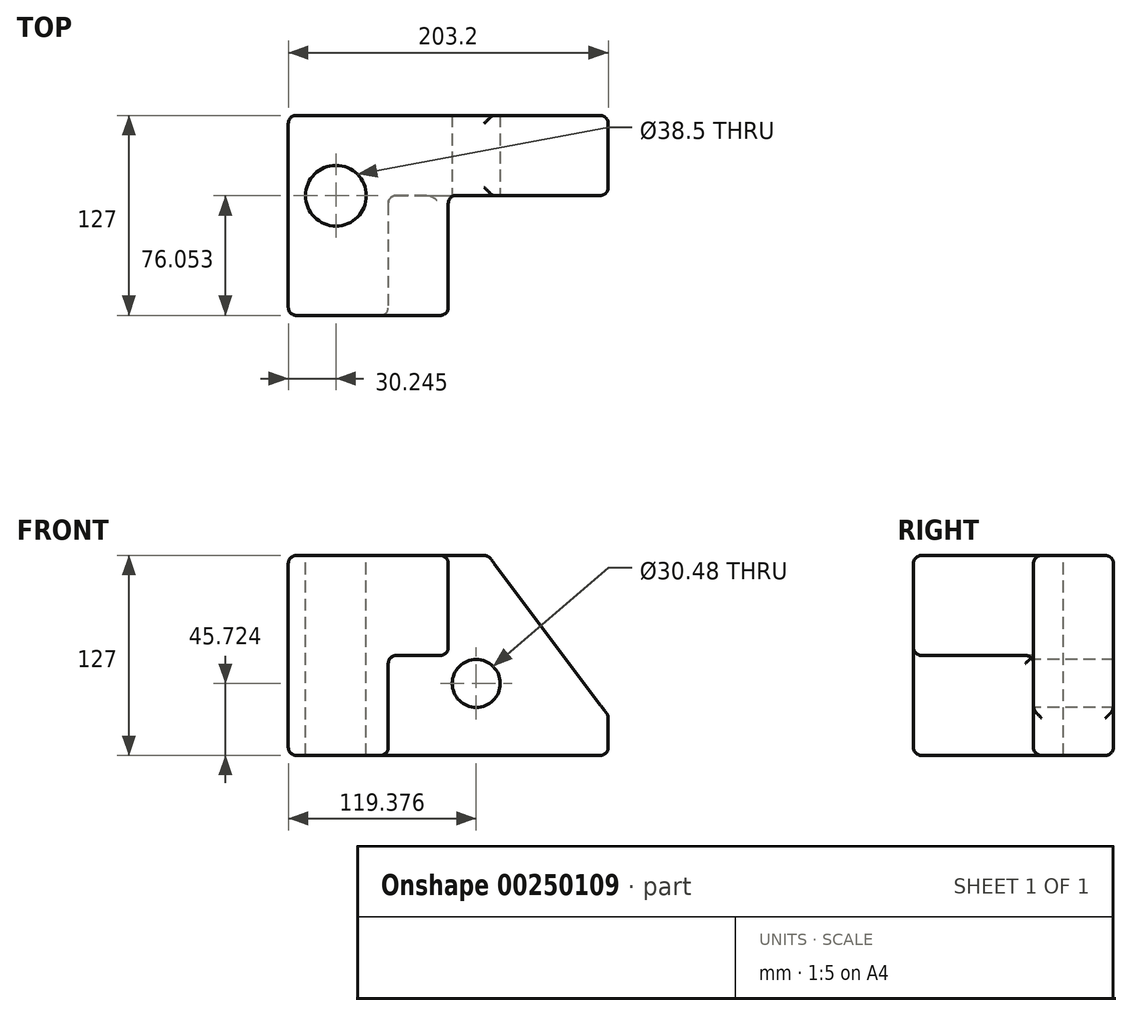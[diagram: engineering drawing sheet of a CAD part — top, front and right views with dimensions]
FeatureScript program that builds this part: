
annotation { "Feature Type Name" : "Feature", "Feature Type Description" : "" }
export const myFeature = defineFeature(function(context is Context, id is Id, definition is map)
    precondition{}
    {
        {
            var Q0;
            Q0=qCreatedBy(makeId("Front.planeOp"),FACE);
            var sketch = newSketch(context, id + "F0", { "sketchPlane" : qUnion([Q0])});
            skLineSegment(sketch, "E0.bottom", {"start": v(-105.93, 60.95) * mm, "end": v(97.27, 60.95) * mm});
            skLineSegment(sketch, "E0.top", {"start": v(-105.93, -66.05) * mm, "end": v(97.27, -66.05) * mm});
            skLineSegment(sketch, "E0.left", {"start": v(-105.93, 60.95) * mm, "end": v(-105.93, -66.05) * mm});
            skLineSegment(sketch, "E0.right", {"start": v(97.27, 60.95) * mm, "end": v(97.27, -66.05) * mm});
            skSolve(sketch);
        }
        {
            var Q0;
            Q0=makeQuery(id+"F0.imprint","IMPRINT",FACE,{"disambiguationData":[TD([[makeQuery(id+"F0.imprint","IMPRINT",EDGE,{"derivedFrom":sQuery(id+"F0.wireOp",EDGE,"E0.bottom")}),-1.0]])]});
            extrude(context, id + "F1", {"entities" : qUnion([Q0]), "depth" : 127 * mm});
        }
        {
            var Q0;
            Q0=makeQuery(id+"F1.opExtrude","CAP_FACE",FACE,{"disambiguationData":[OSD([sQuery(id+"F0.wireOp",EDGE,"E0.bottom"),sQuery(id+"F0.wireOp",EDGE,"E0.top"),sQuery(id+"F0.wireOp",EDGE,"E0.left"),sQuery(id+"F0.wireOp",EDGE,"E0.right")])],"isStart":false});
            var sketch = newSketch(context, id + "F2", { "sketchPlane" : qUnion([Q0])});
            skLineSegment(sketch, "E1", {"start": v(-105.93, -66.05) * mm, "end": v(-105.93, 60.95) * mm});
            skLineSegment(sketch, "E2", {"start": v(-105.93, 60.95) * mm, "end": v(-4.33, 60.95) * mm});
            skLineSegment(sketch, "E3", {"start": v(-4.33, 60.95) * mm, "end": v(-4.33, -2.55) * mm});
            skLineSegment(sketch, "E4", {"start": v(-4.33, -2.55) * mm, "end": v(-42.43, -2.55) * mm});
            skLineSegment(sketch, "E5", {"start": v(-42.43, -2.55) * mm, "end": v(-42.43, -66.05) * mm});
            skLineSegment(sketch, "E6", {"start": v(-42.43, -66.05) * mm, "end": v(-105.93, -66.05) * mm});
            skSolve(sketch);
        }
        {
            var Q0;
            {var subQ2=sQuery(id+"F2.wireOp",EDGE,"E3");Q0=makeQuery(id+"F2.imprint","IMPRINT",FACE,{"disambiguationData":[TD([[makeQuery(id+"F2.imprint","IMPRINT",EDGE,{"derivedFrom":subQ2}),1.0]])]});}
            extrude(context, id + "F3", {"entities" : qUnion([Q0]), "operationType" : NewBodyOperationType.REMOVE, "oppositeDirection" : true, "depth" : 76.2 * mm});
        }
        {
            var Q0;
            Q0=makeQuery(id+"F1.opExtrude","SWEPT_EDGE",EDGE,{"disambiguationData":[OSD([sQuery(id+"F0.wireOp",EDGE,"E0.bottom"),sQuery(id+"F0.wireOp",EDGE,"E0.right")])]});
            chamfer(context, id + "F4", {"entities" : qUnion([Q0]), "chamferType" : ChamferType.TWO_OFFSETS, "width1" : 76.2 * mm, "oppositeDirection" : false, "width2" : 101.6 * mm, "tangentPropagation" : true});
        }
        {
            var Q0;
            Q0=makeQuery(id+"F1.opExtrude","CAP_FACE",FACE,{"disambiguationData":[OSD([sQuery(id+"F0.wireOp",EDGE,"E0.bottom"),sQuery(id+"F0.wireOp",EDGE,"E0.top"),sQuery(id+"F0.wireOp",EDGE,"E0.left"),sQuery(id+"F0.wireOp",EDGE,"E0.right")])],"isStart":false});
            var Q1;
            Q1=makeQuery(id+"F1.opExtrude","SWEPT_FACE",FACE,{"disambiguationData":[OSD([sQuery(id+"F0.wireOp",EDGE,"E0.bottom")])]});
            var Q2;
            Q2=makeQuery(id+"F3.boolean.opBoolean","COPY",FACE,{"derivedFrom":makeQuery(id+"F3.opExtrude","SWEPT_FACE",FACE,{"disambiguationData":[OSD([sQuery(id+"F2.wireOp",EDGE,"E3")])]})});
            var Q3;
            Q3=makeQuery(id+"F3.boolean.opBoolean","COPY",FACE,{"derivedFrom":makeQuery(id+"F3.opExtrude","SWEPT_FACE",FACE,{"disambiguationData":[OSD([sQuery(id+"F2.wireOp",EDGE,"E5")])]})});
            var Q4;
            Q4=makeQuery(id+"F1.opExtrude","SWEPT_FACE",FACE,{"disambiguationData":[OSD([sQuery(id+"F0.wireOp",EDGE,"E0.right")])]});
            var Q5;
            Q5=makeQuery(id+"F1.opExtrude","SWEPT_FACE",FACE,{"disambiguationData":[OSD([sQuery(id+"F0.wireOp",EDGE,"E0.left")])]});
            var Q6;
            Q6=makeQuery(id+"F1.opExtrude","SWEPT_FACE",FACE,{"disambiguationData":[OSD([sQuery(id+"F0.wireOp",EDGE,"E0.top")])]});
            fillet(context, id + "F5", {"entities" : qUnion([Q0, Q1, Q2, Q3, Q4, Q5, Q6]), "radius" : 5.08 * mm, "tangentPropagation" : true, "allowEdgeOverflow" : false});
        }
        {
            var Q0;
            Q0=makeQuery(id+"F3.boolean.opBoolean","COPY",FACE,{"derivedFrom":makeQuery(id+"F3.opExtrude","CAP_FACE",FACE,{"disambiguationData":[OSD([sQuery(id+"F0.wireOp",EDGE,"E0.bottom"),sQuery(id+"F0.wireOp",EDGE,"E0.top"),sQuery(id+"F0.wireOp",EDGE,"E0.right"),sQuery(id+"F2.wireOp",EDGE,"E3"),sQuery(id+"F2.wireOp",EDGE,"E4"),sQuery(id+"F2.wireOp",EDGE,"E5")])],"isStart":false})});
            var sketch = newSketch(context, id + "F6", { "sketchPlane" : qUnion([Q0])});
            skCircle(sketch, "E7", {"center": v(13.45, -20.33) * mm, "radius": 15.24 * mm});
            skSolve(sketch);
        }
        {
            var Q0;
            Q0=makeQuery(id+"F6.imprint","IMPRINT",FACE,{"disambiguationData":[TD([[makeQuery(id+"F6.imprint","IMPRINT",EDGE,{"derivedFrom":sQuery(id+"F6.wireOp",EDGE,"E7")}),1.0]])]});
            var Q1;
            Q1=makeQuery(id+"F1.opExtrude","CAP_FACE",FACE,{"disambiguationData":[OSD([sQuery(id+"F0.wireOp",EDGE,"E0.bottom"),sQuery(id+"F0.wireOp",EDGE,"E0.top"),sQuery(id+"F0.wireOp",EDGE,"E0.left"),sQuery(id+"F0.wireOp",EDGE,"E0.right")])],"isStart":true});
            extrude(context, id + "F7", {"entities" : qUnion([Q0]), "operationType" : NewBodyOperationType.REMOVE, "endBound" : BoundingType.UP_TO_SURFACE, "oppositeDirection" : true, "endBoundEntityFace" : qUnion([Q1]), "depth" : 25.4 * mm});
        }
        {
            var Q0;
            Q0=makeQuery(id+"F1.opExtrude","SWEPT_FACE",FACE,{"disambiguationData":[OSD([sQuery(id+"F0.wireOp",EDGE,"E0.bottom")])]});
            var sketch = newSketch(context, id + "F8", { "sketchPlane" : qUnion([Q0])});
            skCircle(sketch, "E8", {"center": v(-75.69, -50.95) * mm, "radius": 19.25 * mm});
            skSolve(sketch);
        }
        {
            var Q0;
            Q0=makeQuery(id+"F8.imprint","IMPRINT",FACE,{"disambiguationData":[TD([[makeQuery(id+"F8.imprint","IMPRINT",EDGE,{"derivedFrom":sQuery(id+"F8.wireOp",EDGE,"E8")}),1.0]])]});
            var Q1;
            Q1=makeQuery(id+"F1.opExtrude","SWEPT_FACE",FACE,{"disambiguationData":[OSD([sQuery(id+"F0.wireOp",EDGE,"E0.top")])]});
            extrude(context, id + "F9", {"entities" : qUnion([Q0]), "operationType" : NewBodyOperationType.REMOVE, "endBound" : BoundingType.UP_TO_SURFACE, "oppositeDirection" : true, "endBoundEntityFace" : qUnion([Q1]), "depth" : 25.4 * mm});
        }
    });
